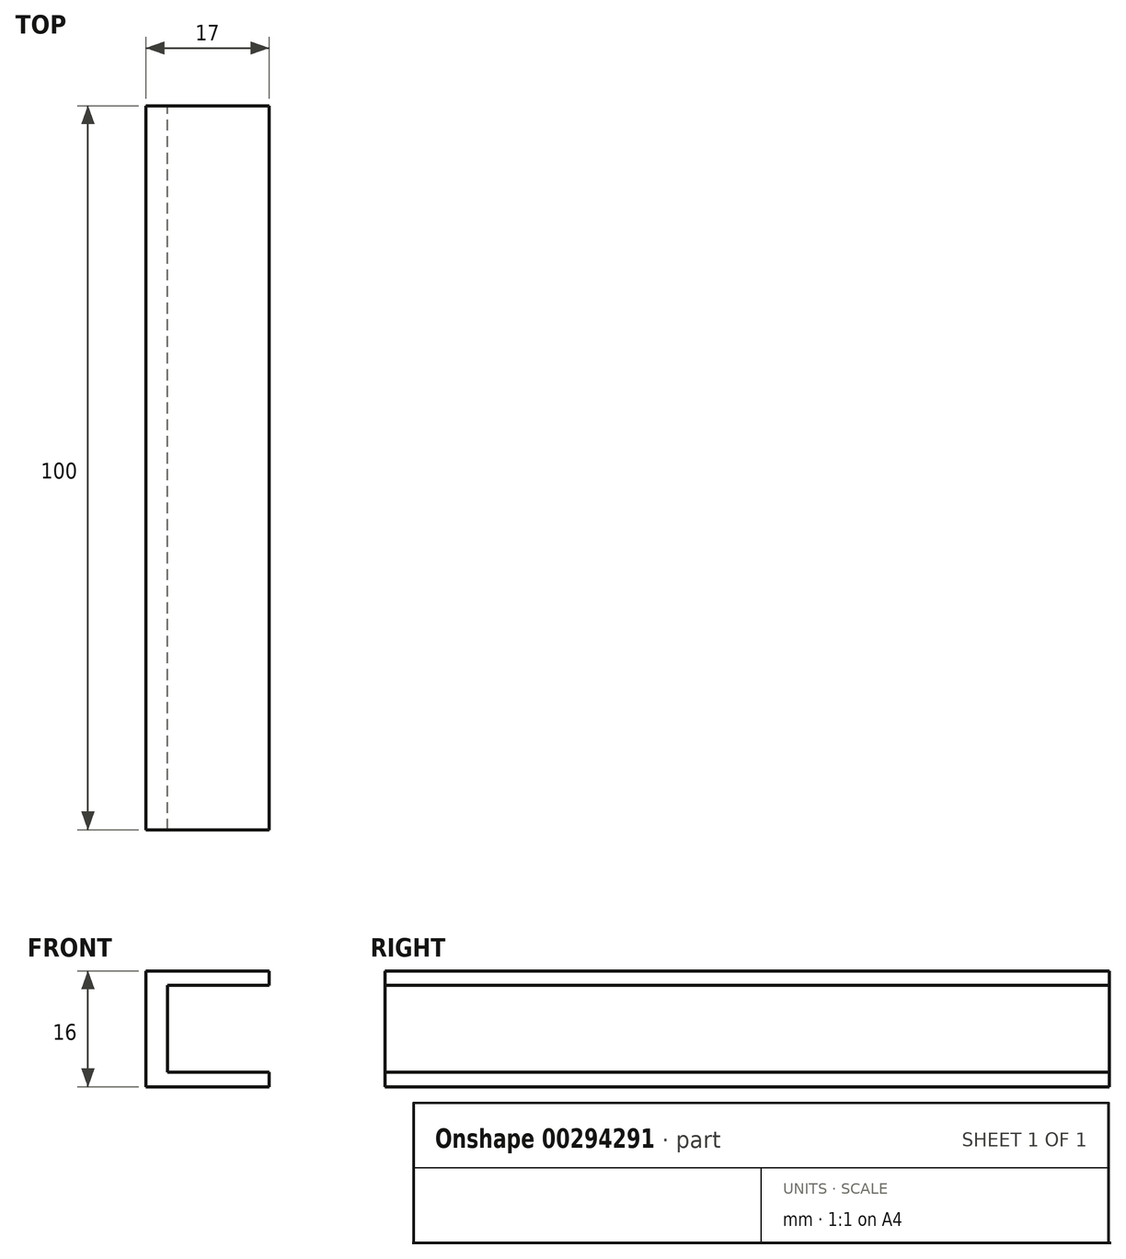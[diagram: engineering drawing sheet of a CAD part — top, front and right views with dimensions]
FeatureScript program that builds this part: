
annotation { "Feature Type Name" : "Feature", "Feature Type Description" : "" }
export const myFeature = defineFeature(function(context is Context, id is Id, definition is map)
    precondition{}
    {
        {
            var Q0;
            Q0=qCreatedBy(makeId("Front.planeOp"),FACE);
            var sketch = newSketch(context, id + "F0", { "sketchPlane" : qUnion([Q0])});
            skLineSegment(sketch, "E0", {"start": v(0, 0) * mm, "end": v(-17, 0) * mm});
            skLineSegment(sketch, "E1", {"start": v(-17, 0) * mm, "end": v(-17, 16) * mm});
            skLineSegment(sketch, "E2", {"start": v(-17, 16) * mm, "end": v(0, 16) * mm});
            skLineSegment(sketch, "E3", {"start": v(0, 16) * mm, "end": v(0, 14) * mm});
            skLineSegment(sketch, "E4", {"start": v(0, 14) * mm, "end": v(-14, 14) * mm});
            skLineSegment(sketch, "E5", {"start": v(-14, 14) * mm, "end": v(-14, 2) * mm});
            skLineSegment(sketch, "E6", {"start": v(-14, 2) * mm, "end": v(0, 2) * mm});
            skLineSegment(sketch, "E7", {"start": v(0, 2) * mm, "end": v(0, 0) * mm});
            skSolve(sketch);
        }
        {
            var Q0;
            Q0 = qSketchRegion(id + "F0", true);
            extrude(context, id + "F1", {"entities" : qUnion([Q0]), "depth" : 100 * mm});
        }
    });
